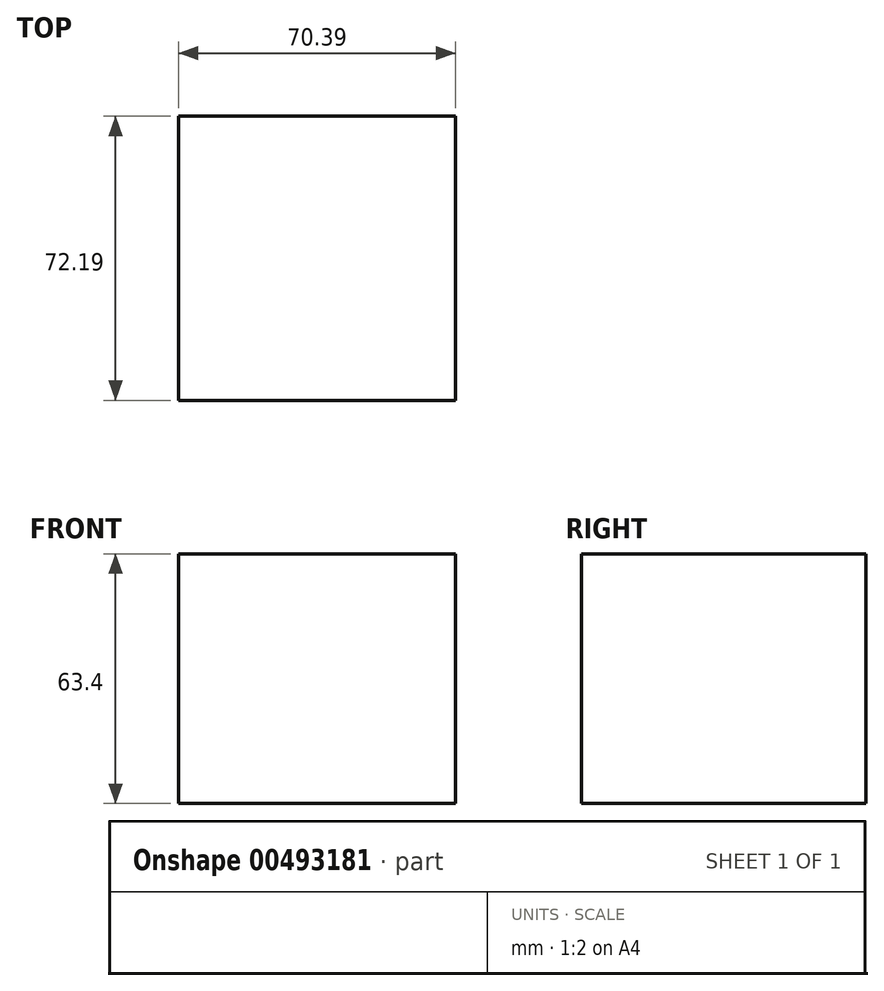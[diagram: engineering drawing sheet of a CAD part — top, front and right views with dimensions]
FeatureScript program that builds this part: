
annotation { "Feature Type Name" : "Feature", "Feature Type Description" : "" }
export const myFeature = defineFeature(function(context is Context, id is Id, definition is map)
    precondition{}
    {
        {
            var Q0;
            Q0=qCreatedBy(makeId("Top.planeOp"),FACE);
            var sketch = newSketch(context, id + "F0", { "sketchPlane" : qUnion([Q0])});
            skLineSegment(sketch, "E0.bottom", {"start": v(-25, 19.6) * mm, "end": v(45.38, 19.6) * mm});
            skLineSegment(sketch, "E0.top", {"start": v(-25, -52.58) * mm, "end": v(45.38, -52.58) * mm});
            skLineSegment(sketch, "E0.left", {"start": v(-25, 19.6) * mm, "end": v(-25, -52.58) * mm});
            skLineSegment(sketch, "E0.right", {"start": v(45.38, 19.6) * mm, "end": v(45.38, -52.58) * mm});
            skSolve(sketch);
        }
        {
            var Q0;
            Q0=makeQuery(id+"F0.imprint","IMPRINT",FACE,{"disambiguationData":[TD([[makeQuery(id+"F0.imprint","IMPRINT",EDGE,{"derivedFrom":sQuery(id+"F0.wireOp",EDGE,"E0.bottom")}),-1.0]])]});
            extrude(context, id + "F1", {"entities" : qUnion([Q0]), "depth" : 63.4 * mm});
        }
    });
